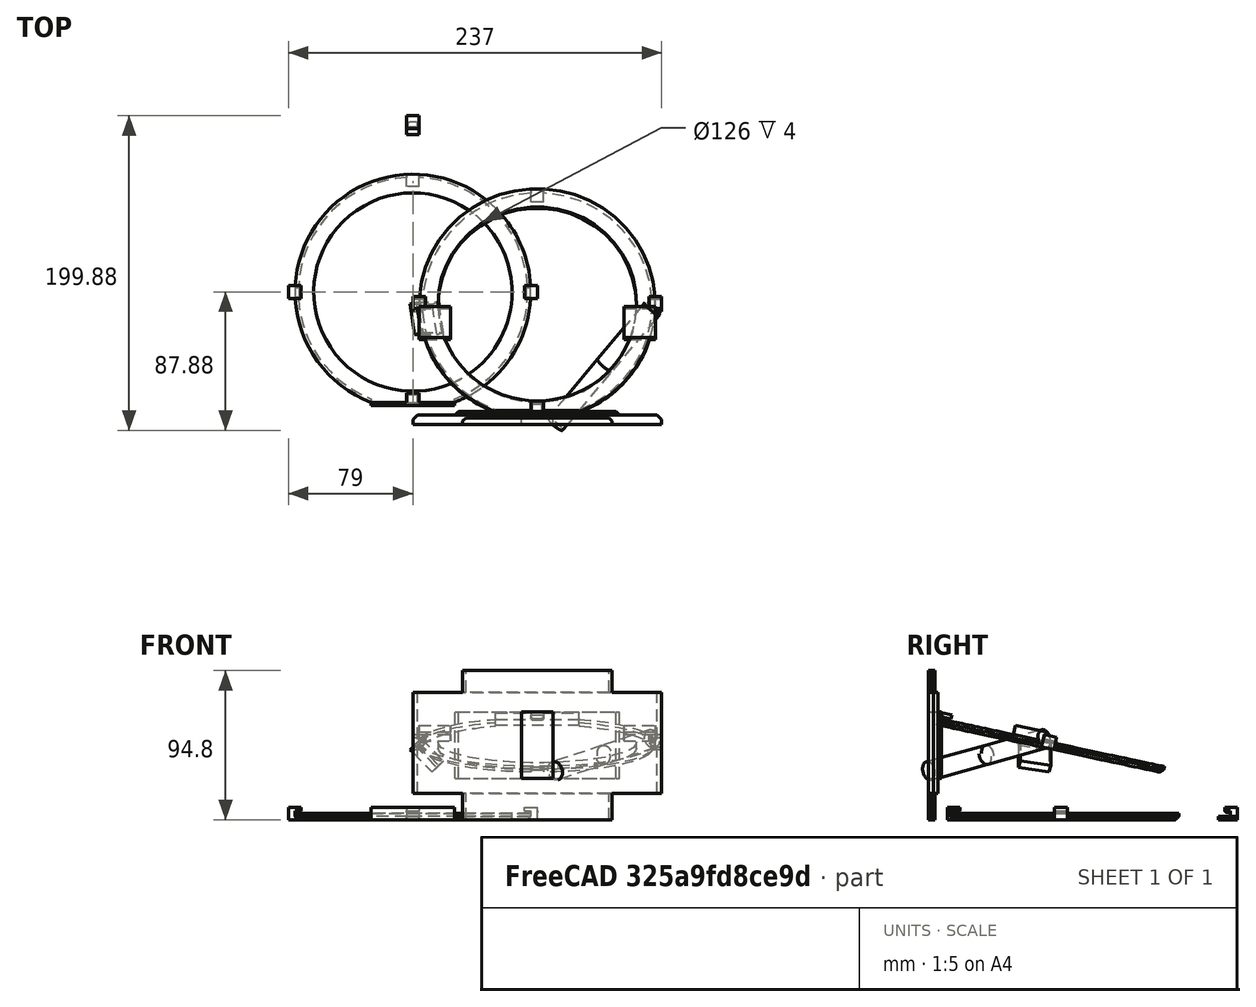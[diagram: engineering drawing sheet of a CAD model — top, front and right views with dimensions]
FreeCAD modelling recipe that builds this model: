
FCSTD DOCUMENT  (FreeCAD 0.19R0.19.2)
Label: waferHolder_019
License: All rights reserved
LicenseURL: http://en.wikipedia.org/wiki/All_rights_reserved
objects: Part::Box×36, Part::Chamfer×28, Part::MultiFuse×12, Part::Cut×10, Part::Cylinder×8, Sketcher::SketchObject×7, Part::Extrusion×7, Part::Fuse×2, App::MeasureDistance×1, Part::Mirroring×1
note: 111 computed .brp shape members not serialized (recipe doc carries the construction recipe); baked Part::Feature solids carry a one-line shape summary decoded from their .brp

FEATURE [Part::Box] Box003  label="bitHolderTop"
  AttacherType = Attacher::AttachEngine3D
  Height = 2
  Length = 8
  Placement = pos=(-4,100,0) rot=(0,0,1;0rad)
  Width = 12
FEATURE [Part::Box] Box008  label="holderBitLeft003"
  AttacherType = Attacher::AttachEngine3D
  Height = 2
  Length = 8
  Placement = pos=(-4,71,2) rot=(0,0,1;0rad)
  Width = 8
FEATURE [Part::Box] Box009  label="bitHolderTopCutout001"
  AttacherType = Attacher::AttachEngine3D
  Height = 4
  Length = 8
  Placement = pos=(-4,67,-2) rot=(0,0,1;0rad)
  Width = 12
FEATURE [Sketcher::SketchObject] Sketch002
  FullyConstrained = true
  sketch-geometry (3):
    g0: Circle CenterX=-3.1415e-12 CenterY=5.6243e-12 CenterZ=0 NormalX=0 NormalY=0 NormalZ=1 AngleXU=0 Radius=63
    g1: ArcOfCircle CenterX=-3.1415e-12 CenterY=5.6243e-12 CenterZ=0 NormalX=0 NormalY=0 NormalZ=1 AngleXU=0 Radius=74.8482 StartAngle=5.07429 EndAngle=10.6337
    g2: LineSegment StartX=-26.5 StartY=-70.0001 StartZ=0 EndX=26.5 EndY=-70.0001 EndZ=0
  constraints (6):
    c: Block(g0)
    c: Coincident(g1,g0)
    c: Block(g1)
    c: Coincident(g2,g1)
    c: Coincident(g2,g1)
    c: Horizontal(g2)
FEATURE [Part::Extrusion] Extrude002  label="mainHolderRing003"
  Base = -> Sketch002
  Dir = (0,0,1)
  DirMode = 2
  FaceMakerClass = Part::FaceMakerBullseye
  LengthFwd = 4
  LengthRev = 0
  Solid = true
  Symmetric = false
FEATURE [Part::Chamfer] Chamfer001
  Base = -> Extrude002
  Edges = 1 edges r=2: [Edge3]
FEATURE [Part::Cut] Cut002  label="mainHolderRing004"
  Base = -> Chamfer001
  Tool = -> Box009
FEATURE [Part::Cut] Cut003  label="bitHolderTop001"
  Base = -> Box008
  Tool = -> Cut002
FEATURE [Part::Box] Box010  label="holderBitLeft004"
  AttacherType = Attacher::AttachEngine3D
  Height = 2
  Length = 8
  Placement = pos=(-4,71,2) rot=(0,0,1;0rad)
  Width = 8
FEATURE [Part::Box] Box011  label="bitHolderTopCutout002"
  AttacherType = Attacher::AttachEngine3D
  Height = 4
  Length = 8
  Placement = pos=(-4,67,-2) rot=(0,0,1;0rad)
  Width = 12
FEATURE [Sketcher::SketchObject] Sketch003
  FullyConstrained = true
  sketch-geometry (3):
    g0: Circle CenterX=-3.1415e-12 CenterY=5.6243e-12 CenterZ=0 NormalX=0 NormalY=0 NormalZ=1 AngleXU=0 Radius=63
    g1: ArcOfCircle CenterX=-3.1415e-12 CenterY=5.6243e-12 CenterZ=0 NormalX=0 NormalY=0 NormalZ=1 AngleXU=0 Radius=74.8482 StartAngle=5.07429 EndAngle=10.6337
    g2: LineSegment StartX=-26.5 StartY=-70.0001 StartZ=0 EndX=26.5 EndY=-70.0001 EndZ=0
  constraints (6):
    c: Block(g0)
    c: Coincident(g1,g0)
    c: Block(g1)
    c: Coincident(g2,g1)
    c: Coincident(g2,g1)
    c: Horizontal(g2)
FEATURE [Part::Extrusion] Extrude003  label="mainHolderRing006"
  Base = -> Sketch003
  Dir = (0,0,1)
  DirMode = 2
  FaceMakerClass = Part::FaceMakerBullseye
  LengthFwd = 4
  LengthRev = 0
  Solid = true
  Symmetric = false
FEATURE [Part::Chamfer] Chamfer002
  Base = -> Extrude003
  Edges = 1 edges r=2: [Edge3]
FEATURE [Part::Cut] Cut005  label="mainHolderRing005"
  Base = -> Chamfer002
  Tool = -> Box011
FEATURE [Part::Cut] Cut004  label="bitHolderTop002"
  Base = -> Box010
  Placement = pos=(0,0,2) rot=(0,0,1;0rad)
  Tool = -> Cut005
FEATURE [Part::Box] Box012  label="holderBitLeft005"
  AttacherType = Attacher::AttachEngine3D
  Height = 2
  Length = 8
  Placement = pos=(-4,71,2) rot=(0,0,1;0rad)
  Width = 8
FEATURE [Part::Box] Box013  label="bitHolderTopCutout003"
  AttacherType = Attacher::AttachEngine3D
  Height = 4
  Length = 8
  Placement = pos=(-4,67,-2) rot=(0,0,1;0rad)
  Width = 12
FEATURE [Sketcher::SketchObject] Sketch004
  FullyConstrained = true
  sketch-geometry (3):
    g0: Circle CenterX=-3.1415e-12 CenterY=5.6243e-12 CenterZ=0 NormalX=0 NormalY=0 NormalZ=1 AngleXU=0 Radius=63
    g1: ArcOfCircle CenterX=-3.1415e-12 CenterY=5.6243e-12 CenterZ=0 NormalX=0 NormalY=0 NormalZ=1 AngleXU=0 Radius=74.8482 StartAngle=5.07429 EndAngle=10.6337
    g2: LineSegment StartX=-26.5 StartY=-70.0001 StartZ=0 EndX=26.5 EndY=-70.0001 EndZ=0
  constraints (6):
    c: Block(g0)
    c: Coincident(g1,g0)
    c: Block(g1)
    c: Coincident(g2,g1)
    c: Coincident(g2,g1)
    c: Horizontal(g2)
FEATURE [Part::Extrusion] Extrude004  label="mainHolderRing008"
  Base = -> Sketch004
  Dir = (0,0,1)
  DirMode = 2
  FaceMakerClass = Part::FaceMakerBullseye
  LengthFwd = 4
  LengthRev = 0
  Solid = true
  Symmetric = false
FEATURE [Part::Chamfer] Chamfer003
  Base = -> Extrude004
  Edges = 1 edges r=2: [Edge3]
FEATURE [Part::Cut] Cut007  label="mainHolderRing007"
  Base = -> Chamfer003
  Tool = -> Box013
FEATURE [Part::Cut] Cut006  label="bitHolderTop003"
  Base = -> Box012
  Placement = pos=(0,0,4) rot=(0,0,1;0rad)
  Tool = -> Cut007
FEATURE [Part::Box] Box014  label="bitHoldertop006"
  AttacherType = Attacher::AttachEngine3D
  Height = 3.4
  Length = 8
  Placement = pos=(-4,71,4.6) rot=(0,0,1;0rad)
  Width = 8
FEATURE [Part::MultiFuse] Fusion001  label="holderTop"
  Placement = pos=(0,33,0) rot=(0,0,1;0rad)
  Shapes = -> [Cut003,Cut004,Cut006,Box014]
FEATURE [Part::Chamfer] Chamfer004
  Base = -> Fusion001
  Edges = 1 edges r=1: [Edge16]
FEATURE [Part::Chamfer] Chamfer009
  Base = -> Chamfer004
  Edges = 1 edges r=1: [Edge1]
FEATURE [Part::Chamfer] Chamfer010
  Base = -> Chamfer009
  Edges = 1 edges r=1: [Edge32]
FEATURE [Part::Box] Box018  label="base001"
  AttacherType = Attacher::AttachEngine3D
  Height = 64.44
  Length = 158
  Placement = pos=(0,-84,16.6) rot=(0,0,1;0rad)
  Width = 6
FEATURE [Part::Box] Box019  label="base002"
  AttacherType = Attacher::AttachEngine3D
  Height = 94.8
  Length = 94.8
  Placement = pos=(31.6,-84,0) rot=(0,0,1;0rad)
  Width = 4
FEATURE [Part::Box] Box020  label="base003"
  AttacherType = Attacher::AttachEngine3D
  Height = 42.44
  Length = 104.28
  Placement = pos=(26.86,-84,26.18) rot=(0,0,1;0rad)
  Width = 8
FEATURE [Part::Chamfer] Chamfer014
  Base = -> Box018
  Edges = 1 edges r=3: [Edge3]
FEATURE [Part::Chamfer] Chamfer015
  Base = -> Chamfer014
  Edges = 1 edges r=3: [Edge15]
FEATURE [Part::Chamfer] Chamfer016
  Base = -> Box019
  Edges = 1 edges r=2: [Edge3]
FEATURE [Part::Chamfer] Chamfer017
  Base = -> Box020
  Edges = 1 edges r=2: [Edge3]
FEATURE [Part::Chamfer] Chamfer018
  Base = -> Chamfer016
  Edges = 1 edges r=2: [Edge15]
FEATURE [Part::Chamfer] Chamfer019
  Base = -> Chamfer017
  Edges = 1 edges r=2: [Edge15]
FEATURE [Part::MultiFuse] Fusion002  label="base004"
  Shapes = -> [Chamfer015,Chamfer018,Chamfer019]
FEATURE [Part::Box] Box021  label="holderBitLeft006"
  AttacherType = Attacher::AttachEngine3D
  Height = 4
  Length = 6
  Placement = pos=(-79,-4,0) rot=(0,0,1;0rad)
  Width = 8
FEATURE [Part::Box] Box022  label="holderBitright003"
  AttacherType = Attacher::AttachEngine3D
  Height = 4
  Length = 6
  Placement = pos=(73,-4,0) rot=(0,0,1;0rad)
  Width = 8
FEATURE [Part::Box] Box023  label="holderBitLeft007"
  AttacherType = Attacher::AttachEngine3D
  Height = 3.4
  Length = 8
  Placement = pos=(-79,-4,4.6) rot=(0,0,1;0rad)
  Width = 8
FEATURE [Part::Box] Box024  label="holderBitRight003"
  AttacherType = Attacher::AttachEngine3D
  Height = 3.4
  Length = 8
  Placement = pos=(71,-4,4.6) rot=(0,0,1;0rad)
  Width = 8
FEATURE [Sketcher::SketchObject] Sketch005
  FullyConstrained = true
  sketch-geometry (3):
    g0: Circle CenterX=-3.1415e-12 CenterY=5.6243e-12 CenterZ=0 NormalX=0 NormalY=0 NormalZ=1 AngleXU=0 Radius=63
    g1: ArcOfCircle CenterX=-3.1415e-12 CenterY=5.6243e-12 CenterZ=0 NormalX=0 NormalY=0 NormalZ=1 AngleXU=0 Radius=74.8482 StartAngle=5.07429 EndAngle=10.6337
    g2: LineSegment StartX=-26.5 StartY=-70.0001 StartZ=0 EndX=26.5 EndY=-70.0001 EndZ=0
  constraints (6):
    c: Block(g0)
    c: Coincident(g1,g0)
    c: Block(g1)
    c: Coincident(g2,g1)
    c: Coincident(g2,g1)
    c: Horizontal(g2)
FEATURE [Part::Box] Box025  label="holderBitLeft008"
  AttacherType = Attacher::AttachEngine3D
  Height = 4
  Length = 8
  Placement = pos=(-79,-4,0) rot=(0,0,1;0rad)
  Width = 8
FEATURE [Part::Box] Box026  label="bitHolderTopCutout004"
  AttacherType = Attacher::AttachEngine3D
  Height = 4
  Length = 8
  Placement = pos=(-4,67,-2) rot=(0,0,1;0rad)
  Width = 12
FEATURE [Part::Extrusion] Extrude006  label="mainHolderRing010"
  Base = -> Sketch005
  Dir = (0,0,1)
  DirMode = 2
  FaceMakerClass = Part::FaceMakerBullseye
  LengthFwd = 4
  LengthRev = 0
  Solid = true
  Symmetric = false
FEATURE [Part::Box] Box027  label="holderBitRight004"
  AttacherType = Attacher::AttachEngine3D
  Height = 4
  Length = 8
  Placement = pos=(71,-4,0) rot=(0,0,1;0rad)
  Width = 8
FEATURE [Part::Chamfer] Chamfer020
  Base = -> Extrude006
  Edges = 1 edges r=2: [Edge3]
FEATURE [Part::Cut] Cut008  label="mainHolderRing011"
  Base = -> Chamfer020
  Tool = -> Box026
FEATURE [Part::MultiFuse] Fusion004  label="holders001"
  Shapes = -> [Box021,Box022]
FEATURE [Sketcher::SketchObject] Sketch006
  FullyConstrained = true
  sketch-geometry (3):
    g0: Circle CenterX=-3.1415e-12 CenterY=5.6243e-12 CenterZ=0 NormalX=0 NormalY=0 NormalZ=1 AngleXU=0 Radius=63
    g1: ArcOfCircle CenterX=-3.1415e-12 CenterY=5.6243e-12 CenterZ=0 NormalX=0 NormalY=0 NormalZ=1 AngleXU=0 Radius=74.8482 StartAngle=5.07429 EndAngle=10.6337
    g2: LineSegment StartX=-26.5 StartY=-70.0001 StartZ=0 EndX=26.5 EndY=-70.0001 EndZ=0
  constraints (6):
    c: Block(g0)
    c: Coincident(g1,g0)
    c: Block(g1)
    c: Coincident(g2,g1)
    c: Coincident(g2,g1)
    c: Horizontal(g2)
FEATURE [Part::Extrusion] Extrude005  label="mainHolderRing009"
  Base = -> Sketch006
  Dir = (0,0,1)
  DirMode = 2
  FaceMakerClass = Part::FaceMakerBullseye
  LengthFwd = 4
  LengthRev = 0
  Solid = true
  Symmetric = false
FEATURE [Part::Cut] Cut009  label="leftAndRightHolderBits001"
  Base = -> Fusion004
  Placement = pos=(0,0,4) rot=(0,0,1;0rad)
  Tool = -> Extrude005
FEATURE [Part::Chamfer] Chamfer021
  Base = -> Box023
  Edges = 1 edges r=1: [Edge8]
FEATURE [Part::Chamfer] Chamfer022
  Base = -> Box024
  Edges = 1 edges r=1: [Edge4]
FEATURE [Part::Chamfer] Chamfer023
  Base = -> Chamfer022
  Edges = 1 edges r=1: [Edge13]
FEATURE [Part::Chamfer] Chamfer024
  Base = -> Chamfer023
  Edges = 1 edges r=1: [Edge5]
FEATURE [Part::Box] Box028  label="holderBottom004"
  AttacherType = Attacher::AttachEngine3D
  Height = 4
  Length = 53
  Placement = pos=(-26.5,-72,0) rot=(0,0,1;0rad)
  Width = 4.5
FEATURE [Part::Chamfer] Chamfer025
  Base = -> Chamfer021
  Edges = 1 edges r=1: [Edge5]
FEATURE [Part::Chamfer] Chamfer026
  Base = -> Chamfer025
  Edges = 1 edges r=1: [Edge16]
FEATURE [Part::Box] Box029  label="holderBottom006"
  AttacherType = Attacher::AttachEngine3D
  Height = 4
  Length = 53
  Placement = pos=(-26.5,-72,4) rot=(0,0,1;0rad)
  Width = 2
FEATURE [Part::Box] Box030  label="holderBottom007"
  AttacherType = Attacher::AttachEngine3D
  Height = 3.4
  Length = 8
  Placement = pos=(-4,-72,4.6) rot=(0,0,1;0rad)
  Width = 8
FEATURE [Part::Chamfer] Chamfer027  label="holderBottom005"
  Base = -> Box030
  Edges = 3 edges r=1: [Edge4,Edge8,Edge11]
FEATURE [Part::MultiFuse] Fusion005  label="removeRingHolder"
  Placement = pos=(79,-8.35,45.4) rot=(1,0,0;6.07375rad)
  Shapes = -> [Box025,Box027,Cut008,Cut009,Chamfer024,Chamfer026,Box028,Box029,Chamfer027]
FEATURE [Part::Box] Box017  label="holderBottom002"
  AttacherType = Attacher::AttachEngine3D
  Height = 3.4
  Length = 8
  Placement = pos=(-4,-72,4.6) rot=(0,0,1;0rad)
  Width = 8
FEATURE [Part::Chamfer] Chamfer013  label="holderBottom003"
  Base = -> Box017
  Edges = 3 edges r=1: [Edge4,Edge8,Edge11]
FEATURE [Part::Box] Box016  label="holderBottom001"
  AttacherType = Attacher::AttachEngine3D
  Height = 4
  Length = 53
  Placement = pos=(-26.5,-72,4) rot=(0,0,1;0rad)
  Width = 2
FEATURE [Part::Box] Box015  label="holderBottom"
  AttacherType = Attacher::AttachEngine3D
  Height = 4
  Length = 53
  Placement = pos=(-26.5,-72,0) rot=(0,0,1;0rad)
  Width = 4.5
FEATURE [Part::Box] Box006  label="holderBitLeft002"
  AttacherType = Attacher::AttachEngine3D
  Height = 3.4
  Length = 8
  Placement = pos=(-79,-4,4.6) rot=(0,0,1;0rad)
  Width = 8
FEATURE [Part::Chamfer] Chamfer005
  Base = -> Box006
  Edges = 1 edges r=1: [Edge8]
FEATURE [Part::Chamfer] Chamfer011
  Base = -> Chamfer005
  Edges = 1 edges r=1: [Edge5]
FEATURE [Part::Chamfer] Chamfer012
  Base = -> Chamfer011
  Edges = 1 edges r=1: [Edge16]
FEATURE [Part::Box] Box007  label="holderBitRight002"
  AttacherType = Attacher::AttachEngine3D
  Height = 3.4
  Length = 8
  Placement = pos=(71,-4,4.6) rot=(0,0,1;0rad)
  Width = 8
FEATURE [Part::Chamfer] Chamfer006
  Base = -> Box007
  Edges = 1 edges r=1: [Edge4]
FEATURE [Part::Chamfer] Chamfer007
  Base = -> Chamfer006
  Edges = 1 edges r=1: [Edge13]
FEATURE [Part::Chamfer] Chamfer008
  Base = -> Chamfer007
  Edges = 1 edges r=1: [Edge5]
FEATURE [Sketcher::SketchObject] Sketch001
  FullyConstrained = true
  sketch-geometry (3):
    g0: Circle CenterX=-3.1415e-12 CenterY=5.6243e-12 CenterZ=0 NormalX=0 NormalY=0 NormalZ=1 AngleXU=0 Radius=63
    g1: ArcOfCircle CenterX=-3.1415e-12 CenterY=5.6243e-12 CenterZ=0 NormalX=0 NormalY=0 NormalZ=1 AngleXU=0 Radius=74.8482 StartAngle=5.07429 EndAngle=10.6337
    g2: LineSegment StartX=-26.5 StartY=-70.0001 StartZ=0 EndX=26.5 EndY=-70.0001 EndZ=0
  constraints (6):
    c: Block(g0)
    c: Coincident(g1,g0)
    c: Block(g1)
    c: Coincident(g2,g1)
    c: Coincident(g2,g1)
    c: Horizontal(g2)
FEATURE [Part::Extrusion] Extrude001  label="mainHolderRing002"
  Base = -> Sketch001
  Dir = (0,0,1)
  DirMode = 2
  FaceMakerClass = Part::FaceMakerBullseye
  LengthFwd = 4
  LengthRev = 0
  Solid = true
  Symmetric = false
FEATURE [Part::Box] Box005  label="holderBitright002"
  AttacherType = Attacher::AttachEngine3D
  Height = 4
  Length = 6
  Placement = pos=(73,-4,0) rot=(0,0,1;0rad)
  Width = 8
FEATURE [Part::Box] Box004  label="holderBitLeft001"
  AttacherType = Attacher::AttachEngine3D
  Height = 4
  Length = 6
  Placement = pos=(-79,-4,0) rot=(0,0,1;0rad)
  Width = 8
FEATURE [Part::MultiFuse] Fusion  label="holders"
  Shapes = -> [Box004,Box005]
FEATURE [Part::Cut] Cut001  label="leftAndRightHolderBits"
  Base = -> Fusion
  Placement = pos=(0,0,4) rot=(0,0,1;0rad)
  Tool = -> Extrude001
FEATURE [Part::Box] Box001  label="bitHolderTopCutout"
  AttacherType = Attacher::AttachEngine3D
  Height = 4
  Length = 8
  Placement = pos=(-4,67,-2) rot=(0,0,1;0rad)
  Width = 12
FEATURE [Sketcher::SketchObject] Sketch
  FullyConstrained = true
  sketch-geometry (3):
    g0: Circle CenterX=-3.1415e-12 CenterY=5.6243e-12 CenterZ=0 NormalX=0 NormalY=0 NormalZ=1 AngleXU=0 Radius=63
    g1: ArcOfCircle CenterX=-3.1415e-12 CenterY=5.6243e-12 CenterZ=0 NormalX=0 NormalY=0 NormalZ=1 AngleXU=0 Radius=74.8482 StartAngle=5.07429 EndAngle=10.6337
    g2: LineSegment StartX=-26.5 StartY=-70.0001 StartZ=0 EndX=26.5 EndY=-70.0001 EndZ=0
  constraints (6):
    c: Block(g0)
    c: Coincident(g1,g0)
    c: Block(g1)
    c: Coincident(g2,g1)
    c: Coincident(g2,g1)
    c: Horizontal(g2)
FEATURE [Part::Extrusion] Extrude  label="mainHolderRing"
  Base = -> Sketch
  Dir = (0,0,1)
  DirMode = 2
  FaceMakerClass = Part::FaceMakerBullseye
  LengthFwd = 4
  LengthRev = 0
  Solid = true
  Symmetric = false
FEATURE [Part::Chamfer] Chamfer
  Base = -> Extrude
  Edges = 1 edges r=2: [Edge3]
FEATURE [Part::Cut] Cut  label="mainHolderRing001"
  Base = -> Chamfer
  Tool = -> Box001
FEATURE [Part::Box] Box002  label="holderBitRight"
  AttacherType = Attacher::AttachEngine3D
  Height = 4
  Length = 8
  Placement = pos=(71,-4,0) rot=(0,0,1;0rad)
  Width = 8
FEATURE [Part::Box] Box  label="holderBitLeft"
  AttacherType = Attacher::AttachEngine3D
  Height = 4
  Length = 8
  Placement = pos=(-79,-4,0) rot=(0,0,1;0rad)
  Width = 8
FEATURE [Part::MultiFuse] Fusion003  label="ringHolder"
  Shapes = -> [Box,Box002,Cut,Cut001,Chamfer008,Chamfer012,Box015,Box016,Chamfer013]
FEATURE [Part::Cylinder] Cylinder
  Angle = 360
  AttacherType = Attacher::AttachEngine3D
  Height = 50
  Placement = pos=(34.86,-30,47.4) rot=(1,0,0;1.5708rad)
  Radius = 6
FEATURE [Part::Box] Box031  label="base005"
  AttacherType = Attacher::AttachEngine3D
  Height = 42.44
  Length = 20.28
  Placement = pos=(68.86,-84,26.18) rot=(0,0,1;0rad)
  Width = 8
FEATURE [Part::Cylinder] Cylinder001
  Angle = 360
  AttacherType = Attacher::AttachEngine3D
  Height = 50
  Placement = pos=(34.86,-30,47.4) rot=(1,0,0;1.5708rad)
  Radius = 6
FEATURE [Part::MultiFuse] Fusion006
  Placement = pos=(0,0,0) rot=(1,0,0;0.20944rad)
  Shapes = -> [Cylinder001,Cylinder]
FEATURE [Part::Cylinder] Cylinder002
  Angle = 360
  AttacherType = Attacher::AttachEngine3D
  Height = 50
  Placement = pos=(34.86,-30,47.4) rot=(1,0,0;1.5708rad)
  Radius = 6
FEATURE [Part::Cylinder] Cylinder003
  Angle = 360
  AttacherType = Attacher::AttachEngine3D
  Height = 50
  Placement = pos=(34.86,-30,47.4) rot=(1,0,0;1.5708rad)
  Radius = 6
FEATURE [Part::MultiFuse] Fusion007
  Placement = pos=(0,0,0) rot=(1,0,0;0.20944rad)
  Shapes = -> [Cylinder003,Cylinder002]
FEATURE [Part::MultiFuse] Fusion008
  Placement = pos=(-44.06,-5,11.27) rot=(0,0,1;0.698132rad)
  Shapes = -> [Fusion007,Fusion006]
FEATURE [App::MeasureDistance] Distance  label="Distance: 0.65 mm"
  Distance = 0.654413
  P1 = (68.86,-76,67.959)
  P2 = (68.8586,-76,68.6134)
FEATURE [Part::Cylinder] Cylinder004
  Angle = 360
  AttacherType = Attacher::AttachEngine3D
  Height = 50
  Placement = pos=(34.86,-30,47.4) rot=(1,0,0;1.5708rad)
  Radius = 6
FEATURE [Part::Cylinder] Cylinder005
  Angle = 360
  AttacherType = Attacher::AttachEngine3D
  Height = 50
  Placement = pos=(34.86,-30,47.4) rot=(1,0,0;1.5708rad)
  Radius = 6
FEATURE [Part::MultiFuse] Fusion010
  Placement = pos=(0,0,0) rot=(1,0,0;0.20944rad)
  Shapes = -> [Cylinder005,Cylinder004]
FEATURE [Part::Cylinder] Cylinder006
  Angle = 360
  AttacherType = Attacher::AttachEngine3D
  Height = 50
  Placement = pos=(34.86,-30,47.4) rot=(1,0,0;1.5708rad)
  Radius = 6
FEATURE [Part::Cylinder] Cylinder007
  Angle = 360
  AttacherType = Attacher::AttachEngine3D
  Height = 50
  Placement = pos=(34.86,-30,47.4) rot=(1,0,0;1.5708rad)
  Radius = 6
FEATURE [Part::MultiFuse] Fusion009
  Placement = pos=(0,0,0) rot=(1,0,0;0.20944rad)
  Shapes = -> [Cylinder007,Cylinder006]
FEATURE [Part::MultiFuse] Fusion011
  Placement = pos=(-14,-40.82,1.35) rot=(0,0,1;0.698132rad)
  Shapes = -> [Fusion009,Fusion010]
FEATURE [Part::Fuse] Fusion012
  Base = -> Fusion008
  Placement = pos=(-1.7,2,0) rot=(0,0,1;0rad)
  Tool = -> Fusion011
FEATURE [Part::Mirroring] Part__Mirroring  label="Fusion012 (Mirror #1)"
  Base = (0,0,0)
  Normal = (1,0,0)
  Placement = pos=(158,0,0) rot=(0,0,1;0rad)
  Source = -> Fusion012
FEATURE [Part::Box] Box032  label="removeStrutLeft"
  AttacherType = Attacher::AttachEngine3D
  Height = 6
  Length = 20
  Placement = pos=(4,-30.1,54.1) rot=(1,0,0;6.07375rad)
  Width = 20
FEATURE [Part::Box] Box033  label="reoveStrustRight"
  AttacherType = Attacher::AttachEngine3D
  Height = 6
  Length = 20
  Placement = pos=(134,-30.1,54.1) rot=(-1,0,0;0.20944rad)
  Width = 20
FEATURE [Part::Box] Box034  label="removeStrutLeft001"
  AttacherType = Attacher::AttachEngine3D
  Height = 6
  Length = 20
  Placement = pos=(4,-30.1,54.1) rot=(-1,0,0;0.20944rad)
  Width = 20
FEATURE [Part::Box] Box035  label="removeStrutLeft002"
  AttacherType = Attacher::AttachEngine3D
  Height = 6
  Length = 20
  Placement = pos=(4,-30.1,54.1) rot=(-1,0,0;0.20944rad)
  Width = 20
FEATURE [Part::Fuse] Fusion013
  Base = -> Box034
  Placement = pos=(-40,3,12) rot=(0,1,0;0.785398rad)
  Tool = -> Box035
